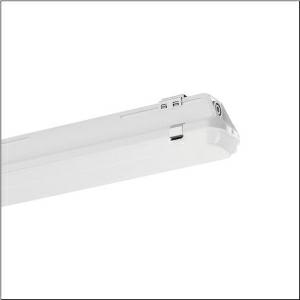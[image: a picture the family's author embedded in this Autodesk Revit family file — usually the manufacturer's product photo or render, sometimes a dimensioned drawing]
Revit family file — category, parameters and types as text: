
# Revit family: monsun_r__21_emergency_51fb207p467b3g_31a7
name_source: partatom
category: Lighting Fixtures
units: mm (PartAtom-declared; Revit-internal decimal feet)

## family parameters
Cut with Voids When Loaded = No
Host = Face
Light Source = No
Part Type = Normal
Room Calculation Point = No
Round Connector Dimension = Use Diameter
Shared = No

## types (1)
- Monsun® 21 emergency (1 x LED, 5460 lm, 42.3 W, 4000K)
    Apparent Load = 42 VA
    CIE Flux Codes = 45 75 93 94 100
    Color Rendering = 80
    Color Temperature = 4000K
    Default Elevation = 1800 mm
    Description = Monsun® 21 emergency, damp-proof luminaire, chain hanger, primary optical cover: enclosure, of PC, light emission: direct distribution, primary light characteristic: symmetric, installation type: vertical mounting, horizontal mounting, surface-mounted, suspended mounting, LED, rated luminous flux: 5.460lm, luminous efficacy: 129lm/W, light colour: 840, colour temperature: 4000K, control gear: ECG, with terminal, 4-pole, max. 2.5mm², mains connection: 220..240V, AC, 50/60Hz, rated input power: 42W, control gear: single battery element, battery: NiCd, 4,5Ah, mains connection: 230V, housing, of glass-fibre reinforced polyester, uncoated, bright grey, length: 1.590mm, width: 90mm, height: 88mm, clip for enclosure, of stainless steel (V2A), ceiling mounting element, of stainless steel (V2A), chain hanger, of stainless steel (V2A), protection rating (complete): IP66, insulation class (complete): insulation class I (protective earthing), certification: CE, UKCA, protection symbol: D, impact resistance: IK08, permissible operating ambient temperature: +5..+25°C, standard: EN 60598-2-1, EN 50419, EN 60598-2-22, corresponds to IFS (International Featured Standards) requirements for safety and quality in the food industry, for indoor or canopied outdoor use, no direct snow, no direct sun, no direct rain, packaging unit: 1 piece
    Height = 89 mm
    Lamp = 1 x LED
    Lamp Light Flux = 5460 lm
    Lamp Power = 42.3 W
    Lamp count = 1
    Length = 1590 mm
    Luminous efficacy = 129 lm/W
    Manufacturer = Siteco
    ModVariant = No
    Model = 51FB207P467B3G
    Mounting Place = Ceiling
    Mounting Type = Pendant
    Number of Poles = 1
    OnlyDefault = Yes
    Power Factor = 1
    Product Name = Monsun® 21 emergency
    Product group = damp-proof luminaire | ceiling pendant
    ProductGroupID = 908
    Protection Class = Protection class I
    Protection Degree = IP 66
    RLX_Detail_Level = 1
    RlxData = <blob elided: 88057 chars, md5=706e636c>
    Socket = socket
    Standby Power = 0 W
    System Light Flux = 5460 lm
    System Power = 42 W
    Type Comments = Product without accessories
    Type Image = l_1006717.jpg
    URL = http://relux.com
    VarID = ---
    Voltage = 0 V
    Weight = 0.00 kg
    Width = 90 mm

## geometry (parser evidence)
native form markers: Blend x4, Sweep x13
no freeform markers — native parametric forms only
